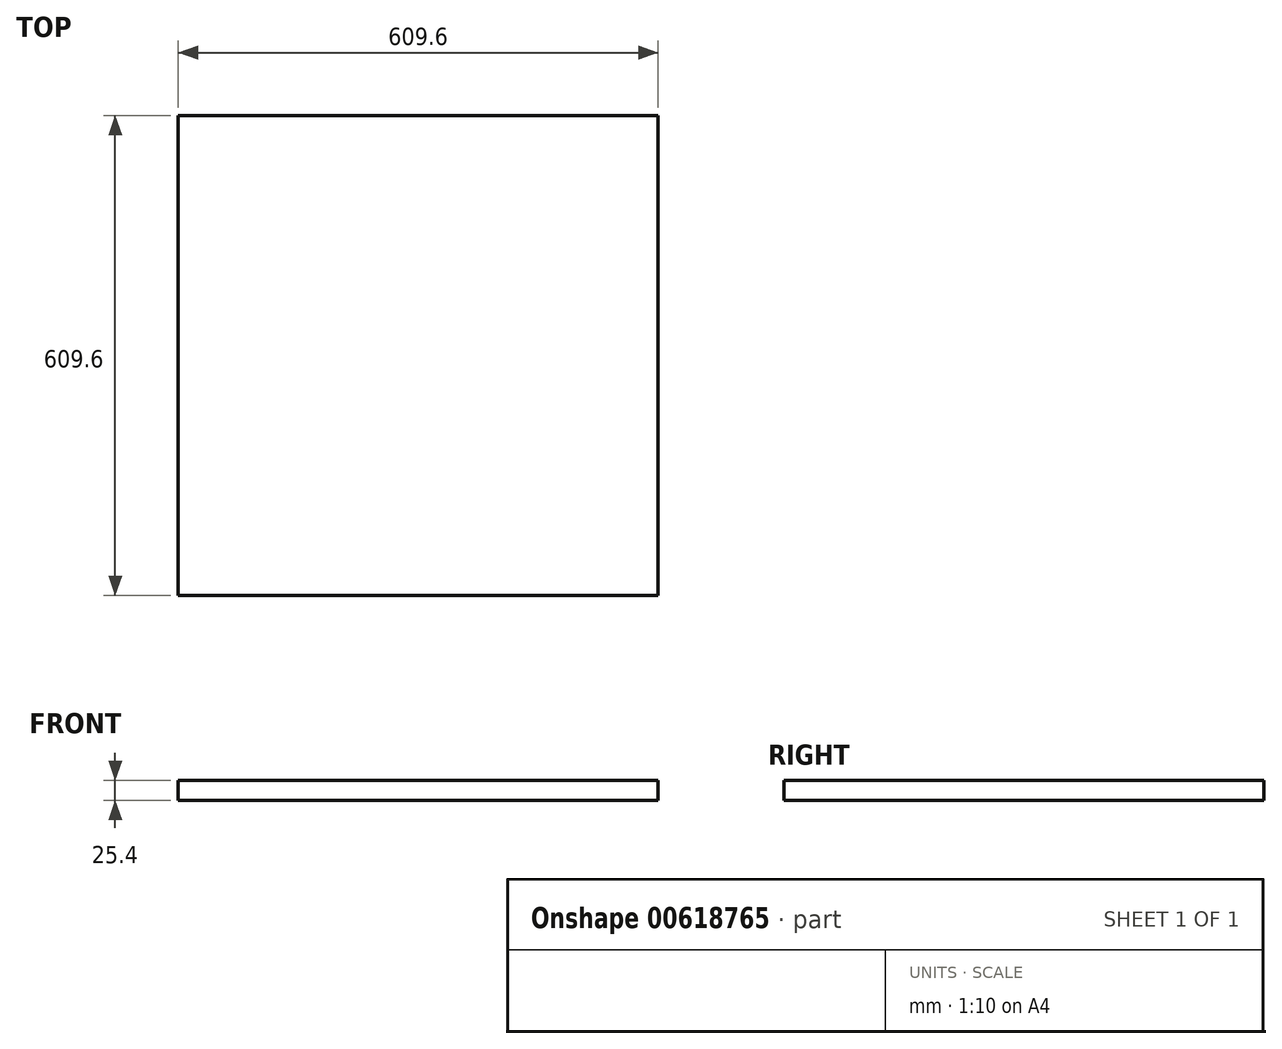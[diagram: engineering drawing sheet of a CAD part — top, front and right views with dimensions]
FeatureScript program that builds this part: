
annotation { "Feature Type Name" : "Feature", "Feature Type Description" : "" }
export const myFeature = defineFeature(function(context is Context, id is Id, definition is map)
    precondition{}
    {
        {
            var Q0;
            Q0=qCreatedBy(makeId("Top.planeOp"),FACE);
            var sketch = newSketch(context, id + "F0", { "sketchPlane" : qUnion([Q0])});
            skLineSegment(sketch, "E0.bottom", {"start": v(304.8, -304.8) * mm, "end": v(-304.8, -304.8) * mm});
            skLineSegment(sketch, "E0.top", {"start": v(304.8, 304.8) * mm, "end": v(-304.8, 304.8) * mm});
            skLineSegment(sketch, "E0.left", {"start": v(304.8, -304.8) * mm, "end": v(304.8, 304.8) * mm});
            skLineSegment(sketch, "E0.right", {"start": v(-304.8, -304.8) * mm, "end": v(-304.8, 304.8) * mm});
            skPoint(sketch, "E0.middle", {"position": v(0, 0) * mm});
            skSolve(sketch);
        }
        {
            var Q0;
            Q0=qCreatedBy(makeId("Right.planeOp"),FACE);
            var sketch = newSketch(context, id + "F1", { "sketchPlane" : qUnion([Q0])});
            skLineSegment(sketch, "E1.bottom", {"start": v(-304.8, -12.7) * mm, "end": v(304.8, -12.7) * mm});
            skLineSegment(sketch, "E1.top", {"start": v(-304.8, 12.7) * mm, "end": v(304.8, 12.7) * mm});
            skLineSegment(sketch, "E1.left", {"start": v(-304.8, -12.7) * mm, "end": v(-304.8, 12.7) * mm});
            skLineSegment(sketch, "E1.right", {"start": v(304.8, -12.7) * mm, "end": v(304.8, 12.7) * mm});
            skPoint(sketch, "E1.middle", {"position": v(0, 0) * mm});
            skSolve(sketch);
        }
        {
            var Q0;
            Q0 = qSketchRegion(id + "F0", true);
            var Q1;
            Q1=sQuery(id+"F1.wireOp",VERTEX,"E1.right.end");
            var Q2;
            Q2=sQuery(id+"F1.wireOp",VERTEX,"E1.bottom.end");
            extrude(context, id + "F2", {"entities" : qUnion([Q0]), "endBound" : BoundingType.UP_TO_VERTEX, "depth" : 25.4 * mm, "endBoundEntityVertex" : qUnion([Q1]), "offsetDistance" : 25.4 * mm, "hasSecondDirection" : true, "secondDirectionBound" : SecondDirectionBoundingType.UP_TO_VERTEX, "secondDirectionOppositeDirection" : true, "secondDirectionDepth" : 25.4 * mm, "secondDirectionBoundEntityVertex" : qUnion([Q2])});
        }
    });
